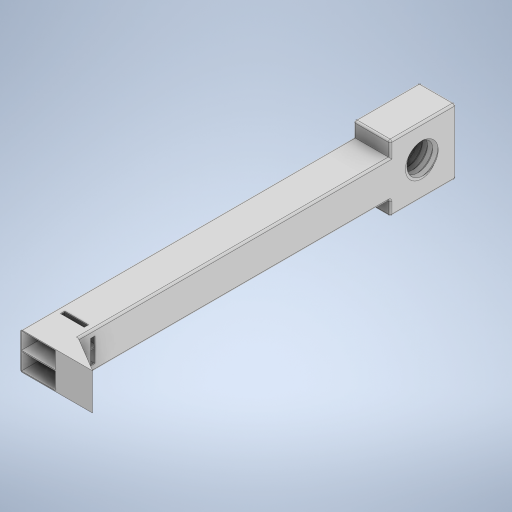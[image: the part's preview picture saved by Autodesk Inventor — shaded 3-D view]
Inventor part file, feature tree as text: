
AUTODESK INVENTOR PART (.ipt)
format: ipt  version: 2024 (Build 280153000, 153)  size: 544,256 bytes
history: native  units: mm
features: sketch x12, extrude x11, other x1, fillet x1
ambient origin geometry x8: Origin, YZ Plane, XZ Plane, XY Plane, X Axis, Y Axis, Z Axis, Center Point
bodies: Volumenkörper1 (feature_tree)
feature tree (25):
  extrude  "Extrusion1"  Depth=10.0mm
  extrude  "Extrusion2"  Depth=10.0mm
  extrude  "Extrusion3"  Depth=18.0mm TaperAngle=0.0deg
  extrude  "Extrusion4"  Depth=9.0mm TaperAngle=0.0deg
  other  "Spirale1"
  extrude  "Extrusion6"  Depth=9.0mm TaperAngle=0.0deg
  extrude  "Extrusion7"  Depth=10.0mm
  extrude  "Extrusion8"  Depth=0.2mm
  extrude  "Extrusion9"  Depth=9.5mm
  fillet  "Rundung2"  Radius=9.5mm
  extrude  "Extrusion10"  Depth=1.5mm
  extrude  "Extrusion11"  Depth=0.5mm
  extrude  "Extrusion13"  Depth=1.5mm
  sketch  "Skizze1"  dims[d0=10.0mm d1=10.0mm]
  sketch  "Skizze2"  dims[d2=91.0mm d3=0.0mm d4=10.0mm]
  sketch  "Skizze3"  dims[d5=18.0mm d6=18.0mm d7=0.0mm]
  sketch  "Skizze4"  dims[d8=10.0mm d9=9.0mm d10=0.0mm]
  sketch  "Skizze5"  dims[d17=7.2mm d18=9.0mm d19=0.0mm]
  sketch  "Skizze7"  dims[d22=1.4mm d23=11.0mm d24=10.0mm d25=0.0mm d26=90.0deg d27=90.0deg d28=0.0mm d29=0.0mm d33=1.7mm]
  sketch  "Skizze8"  dims[d34=60.0deg d35=0.2mm]
  sketch  "Skizze9"  dims[d36=1.0mm d37=0.0mm d39=9.5mm d40=9.5mm]
  sketch  "Skizze10"  dims[d41=9.75mm d42=0.0mm d43=1.5mm]
  sketch  "Skizze11"  dims[d44=1.5mm d45=0.5mm]
  sketch  "Skizze14"  dims[d46=0.5mm d47=1.5mm]
  sketch  "Skizze18"  dims[d48=1.5mm d49=1.5mm d50=1.5mm d51=0.5mm d52=0.5mm d53=1.2mm d54=0.0mm d55=2.0mm d56=0.0mm d57=0.5mm d59=0.5mm d60=10.0mm d61=0.0mm d62=0.0mm d63=0.0mm d64=0.15mm d65=0.15mm d66=11.75mm d67=0.0mm d71=0.25mm d72=1.0mm d73=0.0mm d38=0.0mm]
